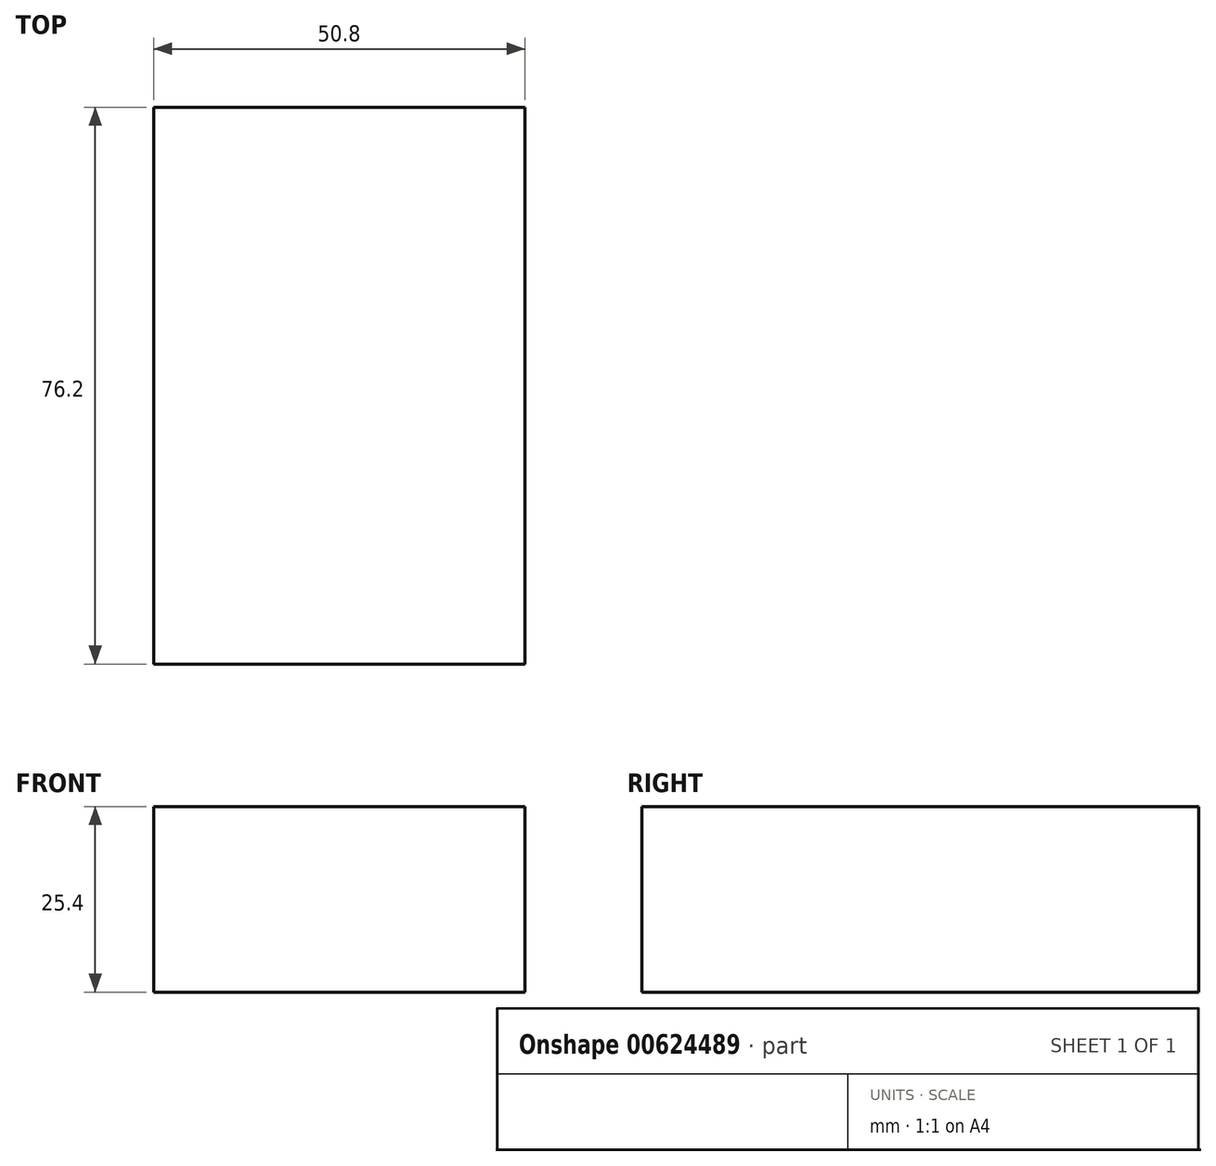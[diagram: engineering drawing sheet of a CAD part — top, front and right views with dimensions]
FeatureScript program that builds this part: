
annotation { "Feature Type Name" : "Feature", "Feature Type Description" : "" }
export const myFeature = defineFeature(function(context is Context, id is Id, definition is map)
    precondition{}
    {
        {
            var Q0;
            Q0=qCreatedBy(makeId("Front.planeOp"),FACE);
            var sketch = newSketch(context, id + "F0", { "sketchPlane" : qUnion([Q0])});
            skLineSegment(sketch, "E0.bottom", {"start": v(0.22, 50.8) * mm, "end": v(127.22, 50.8) * mm});
            skLineSegment(sketch, "E0.top", {"start": v(0.22, 0) * mm, "end": v(127.22, 0) * mm});
            skLineSegment(sketch, "E0.left", {"start": v(0.22, 50.8) * mm, "end": v(0.22, 0) * mm});
            skLineSegment(sketch, "E0.right", {"start": v(127.22, 50.8) * mm, "end": v(127.22, 0) * mm});
            skLineSegment(sketch, "E1.bottom", {"start": v(76.42, 50.8) * mm, "end": v(127.22, 50.8) * mm});
            skLineSegment(sketch, "E1.top", {"start": v(76.42, 25.4) * mm, "end": v(127.22, 25.4) * mm});
            skLineSegment(sketch, "E1.left", {"start": v(76.42, 50.8) * mm, "end": v(76.42, 25.4) * mm});
            skLineSegment(sketch, "E1.right", {"start": v(127.22, 50.8) * mm, "end": v(127.22, 25.4) * mm});
            skSolve(sketch);
        }
        {
            var Q0;
            Q0=makeQuery(id+"F0.imprint","IMPRINT",FACE,{"disambiguationData":[TD([[makeQuery(id+"F0.imprint","IMPRINT",EDGE,{"derivedFrom":sQuery(id+"F0.wireOp",EDGE,"E0.bottom")}),-1.0]])]});
            extrude(context, id + "F1", {"entities" : qUnion([Q0]), "oppositeDirection" : true, "depth" : 76.2 * mm, "offsetDistance" : 25.4 * mm});
        }
        {
            var Q0;
            Q0=makeQuery(id+"F1.opExtrude","SWEPT_FACE",FACE,{"disambiguationData":[OSD([sQuery(id+"F0.wireOp",EDGE,"E1.left")])]});
            var sketch = newSketch(context, id + "F2", { "sketchPlane" : qUnion([Q0])});
            skPoint(sketch, "E2.positionSnap0", {"position": v(38.1, 50.8) * mm});
            skPoint(sketch, "E3.positionSnap0", {"position": v(0, 38.1) * mm});
            skPoint(sketch, "E4", {"position": v(38.1, 38.1) * mm});
            skSolve(sketch);
        }
        {
            var Q0;
            Q0=makeQuery(id+"F1.opExtrude","SWEPT_FACE",FACE,{"disambiguationData":[OSD([sQuery(id+"F0.wireOp",EDGE,"E0.bottom")])]});
            var sketch = newSketch(context, id + "F3", { "sketchPlane" : qUnion([Q0])});
            skPoint(sketch, "E5.positionSnap0", {"position": v(38.32, 76.2) * mm});
            skPoint(sketch, "E6.positionSnap0", {"position": v(0.22, 38.1) * mm});
            skPoint(sketch, "E7", {"position": v(38.32, 0) * mm});
            skPoint(sketch, "E8", {"position": v(38.32, 38.1) * mm});
            skSolve(sketch);
        }
        {
            var Q0;
            Q0=sQuery(id+"F2.wireOp",VERTEX,"E4");
            var Q1;
            Q1=makeQuery(id+"F1.opExtrude","SWEPT_BODY",BODY,{"disambiguationData":[OSD([sQuery(id+"F0.wireOp",EDGE,"E0.bottom"),sQuery(id+"F0.wireOp",EDGE,"E0.top"),sQuery(id+"F0.wireOp",EDGE,"E0.left"),sQuery(id+"F0.wireOp",EDGE,"E0.right"),sQuery(id+"F0.wireOp",EDGE,"E1.top"),sQuery(id+"F0.wireOp",EDGE,"E1.left")])]});
            hole(context, id + "F4", {"style" : HoleStyle.SIMPLE, "endStyle" : HoleEndStyle.THROUGH, "holeDiameter" : 19.05 * mm, "majorDiameter" : 6.35 * mm, "isTappedThrough" : true, "tappedDepth" : 12.7 * mm, "tapClearance" : 3, "locations" : qUnion([Q0]), "scope" : qUnion([Q1])});
        }
        {
            var Q0;
            Q0=sQuery(id+"F3.wireOp",VERTEX,"E8");
            var Q1;
            Q1=makeQuery(id+"F1.opExtrude","SWEPT_BODY",BODY,{"disambiguationData":[OSD([sQuery(id+"F0.wireOp",EDGE,"E0.bottom"),sQuery(id+"F0.wireOp",EDGE,"E0.top"),sQuery(id+"F0.wireOp",EDGE,"E0.left"),sQuery(id+"F0.wireOp",EDGE,"E0.right"),sQuery(id+"F0.wireOp",EDGE,"E1.top"),sQuery(id+"F0.wireOp",EDGE,"E1.left")])]});
            hole(context, id + "F5", {"style" : HoleStyle.SIMPLE, "endStyle" : HoleEndStyle.THROUGH, "holeDiameter" : 19.05 * mm, "majorDiameter" : 6.35 * mm, "isTappedThrough" : true, "tappedDepth" : 12.7 * mm, "tapClearance" : 3, "locations" : qUnion([Q0]), "scope" : qUnion([Q1])});
        }
    });
